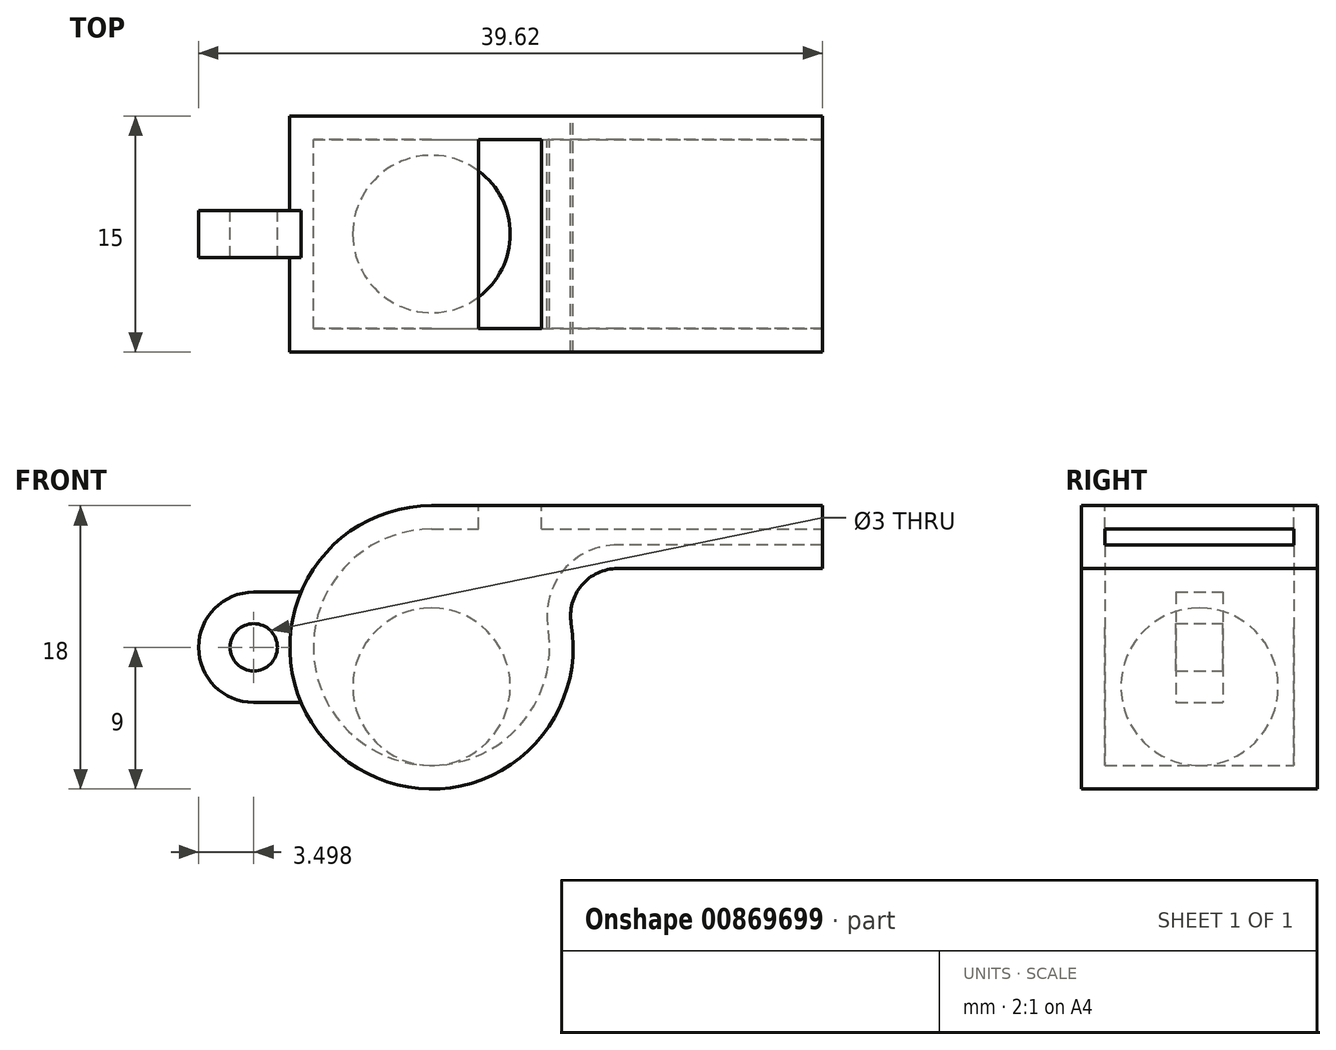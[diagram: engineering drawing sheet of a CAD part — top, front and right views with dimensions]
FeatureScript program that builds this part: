
annotation { "Feature Type Name" : "Feature", "Feature Type Description" : "" }
export const myFeature = defineFeature(function(context is Context, id is Id, definition is map)
    precondition{}
    {
        {
            var Q0;
            Q0=qCreatedBy(makeId("Front.planeOp"),FACE);
            var sketch = newSketch(context, id + "F0", { "sketchPlane" : qUnion([Q0])});
            skArc(sketch, "E0", {"start": v(0, 9) * mm, "mid": v(-5.8, -6.87) * mm, "end": v(8.87, 1.5) * mm});
            skLineSegment(sketch, "E1", {"start": v(0, 9) * mm, "end": v(24.83, 9) * mm});
            skLineSegment(sketch, "E2", {"start": v(24.83, 9) * mm, "end": v(24.83, 5) * mm});
            skLineSegment(sketch, "E3", {"start": v(24.83, 5) * mm, "end": v(11.83, 5) * mm});
            skPoint(sketch, "E4.visualSharp", {"position": v(7.48, 5) * mm});
            skArc(sketch, "E4.filletArc", {"start": v(11.83, 5) * mm, "mid": v(9.54, 3.94) * mm, "end": v(8.87, 1.5) * mm});
            skSolve(sketch);
        }
        {
            var Q0;
            Q0 = qSketchRegion(id + "F0", true);
            extrude(context, id + "F1", {"entities" : qUnion([Q0]), "endBound" : BoundingType.SYMMETRIC, "depth" : 15 * mm, "offsetDistance" : 25 * mm});
        }
        {
            var Q0;
            Q0=makeQuery(id+"F1.opExtrude","SWEPT_FACE",FACE,{"disambiguationData":[OSD([sQuery(id+"F0.wireOp",EDGE,"E2")])]});
            shell(context, id + "F2", {"entities" : qUnion([Q0]), "thickness" : 1.5 * mm});
        }
        {
            var Q0;
            Q0=makeQuery(id+"F1.opExtrude","SWEPT_FACE",FACE,{"disambiguationData":[OSD([sQuery(id+"F0.wireOp",EDGE,"E1")])]});
            var sketch = newSketch(context, id + "F3", { "sketchPlane" : qUnion([Q0])});
            skLineSegment(sketch, "E5.bottom", {"start": v(3, 6) * mm, "end": v(7, 6) * mm});
            skLineSegment(sketch, "E5.top", {"start": v(3, -6) * mm, "end": v(7, -6) * mm});
            skLineSegment(sketch, "E5.left", {"start": v(3, 6) * mm, "end": v(3, -6) * mm});
            skLineSegment(sketch, "E5.right", {"start": v(7, 6) * mm, "end": v(7, -6) * mm});
            skSolve(sketch);
        }
        {
            var Q0;
            Q0=makeQuery(id+"F3.imprint","IMPRINT",FACE,{"disambiguationData":[TD([[makeQuery(id+"F3.imprint","IMPRINT",EDGE,{"derivedFrom":sQuery(id+"F3.wireOp",EDGE,"E5.bottom")}),-1.0]])]});
            extrude(context, id + "F4", {"entities" : qUnion([Q0]), "operationType" : NewBodyOperationType.REMOVE, "oppositeDirection" : true, "depth" : 1.5 * mm, "offsetDistance" : 25 * mm});
        }
        {
            var Q0;
            Q0=qCreatedBy(makeId("Front.planeOp"),FACE);
            var sketch = newSketch(context, id + "F5", { "sketchPlane" : qUnion([Q0])});
            skArc(sketch, "E6", {"start": v(-11.3, 3.5) * mm, "mid": v(-14.8, 0) * mm, "end": v(-11.3, -3.5) * mm});
            skLineSegment(sketch, "E7", {"start": v(-11.3, 3.5) * mm, "end": v(-8.3, 3.5) * mm});
            skLineSegment(sketch, "E8", {"start": v(-11.3, -3.5) * mm, "end": v(-8.3, -3.5) * mm});
            skCircle(sketch, "E9", {"center": v(-11.3, 0) * mm, "radius": 1.5 * mm});
            skLineSegment(sketch, "E10", {"start": v(-8.3, -3.5) * mm, "end": v(-8.3, 3.5) * mm});
            skSolve(sketch);
        }
        {
            var Q0;
            Q0 = qSketchRegion(id + "F5", true);
            extrude(context, id + "F6", {"entities" : qUnion([Q0]), "operationType" : NewBodyOperationType.ADD, "endBound" : BoundingType.SYMMETRIC, "depth" : 3 * mm, "offsetDistance" : 25 * mm});
        }
        {
            var Q0;
            Q0=qCreatedBy(makeId("Front.planeOp"),FACE);
            var sketch = newSketch(context, id + "F7", { "sketchPlane" : qUnion([Q0])});
            skArc(sketch, "E11", {"start": v(0, 2.5) * mm, "mid": v(5, -2.5) * mm, "end": v(0, -7.5) * mm});
            skLineSegment(sketch, "E12", {"start": v(0, 2.5) * mm, "end": v(0, -7.5) * mm});
            skSolve(sketch);
        }
        {
            var Q0;
            Q0 = qSketchRegion(id + "F7", true);
            var Q1;
            Q1=sQuery(id+"F7.wireOp",EDGE,"E12");
            revolve(context, id + "F8", {"surfaceOperationType" : NewSurfaceOperationType.NEW, "entities" : qUnion([Q0]), "axis" : qUnion([Q1]), "revolveType" : RevolveType.FULL});
        }
    });
